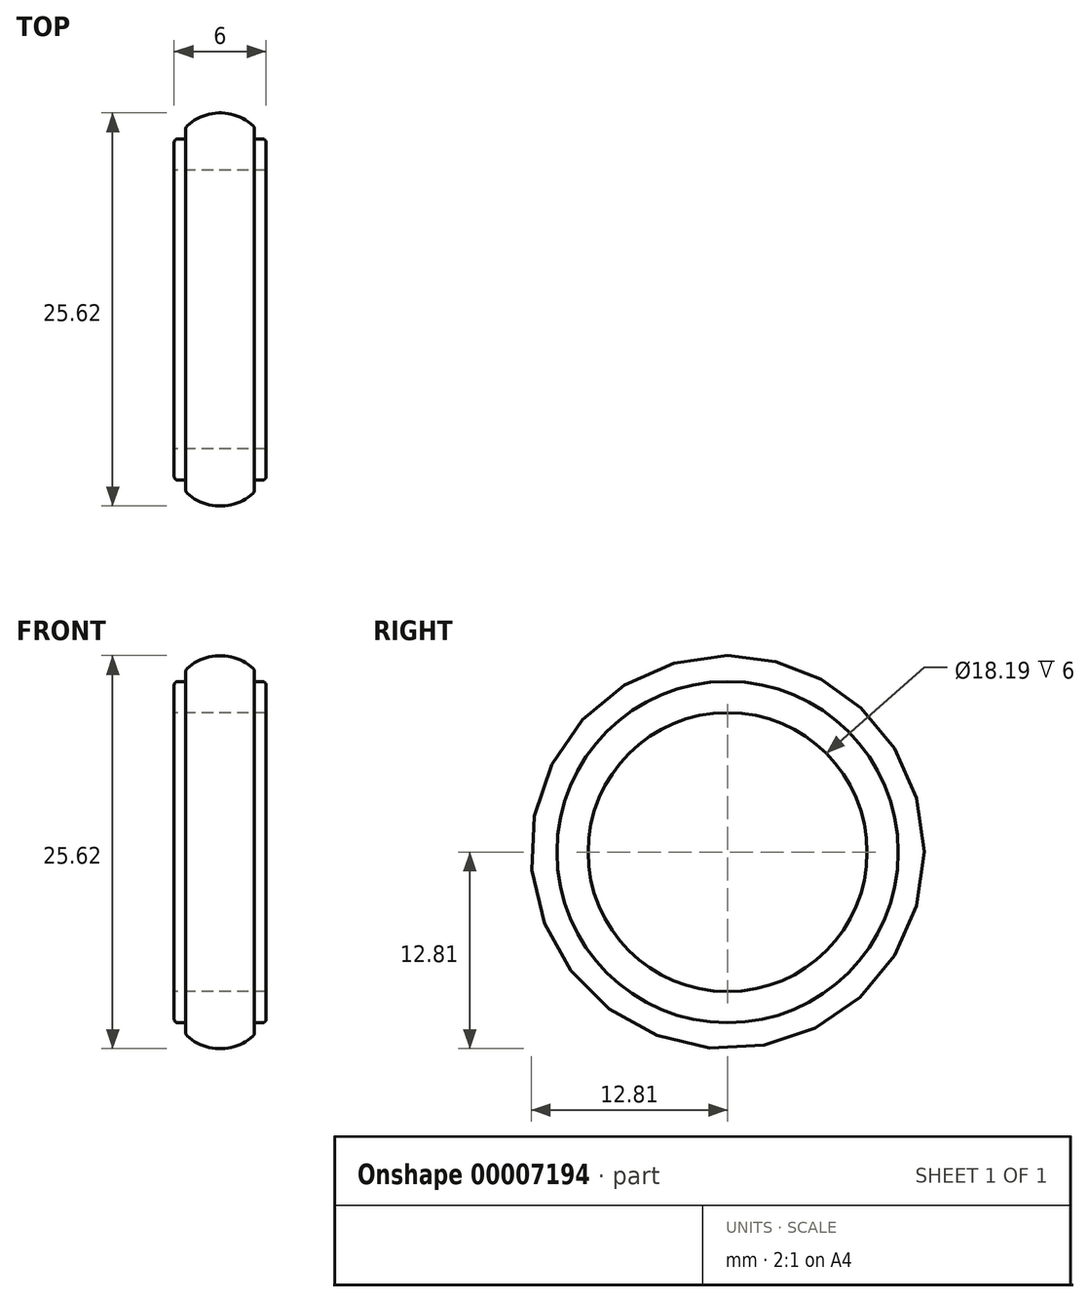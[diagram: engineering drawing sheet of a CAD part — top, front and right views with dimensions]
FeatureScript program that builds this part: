
annotation { "Feature Type Name" : "Feature", "Feature Type Description" : "" }
export const myFeature = defineFeature(function(context is Context, id is Id, definition is map)
    precondition{}
    {
        {
            var Q0;
            Q0=qCreatedBy(makeId("Front.planeOp"),FACE);
            var sketch = newSketch(context, id + "F0", { "sketchPlane" : qUnion([Q0])});
            skLineSegment(sketch, "E0", {"start": v(-3, 9.1) * mm, "end": v(3, 9.1) * mm});
            skLineSegment(sketch, "E1", {"start": v(-3, 9.1) * mm, "end": v(-3, 11.13) * mm});
            skLineSegment(sketch, "E2", {"start": v(3, 11.13) * mm, "end": v(3, 9.1) * mm});
            skLineSegment(sketch, "E3", {"start": v(-3, 11.13) * mm, "end": v(-2.24, 11.13) * mm});
            skLineSegment(sketch, "E4", {"start": v(-2.24, 11.13) * mm, "end": v(-2.24, 11.89) * mm});
            skLineSegment(sketch, "E5", {"start": v(2.24, 11.89) * mm, "end": v(2.24, 11.13) * mm});
            skLineSegment(sketch, "E6", {"start": v(2.24, 11.13) * mm, "end": v(3, 11.13) * mm});
            skArc(sketch, "E7", {"start": v(2.24, 11.89) * mm, "mid": v(0, 12.81) * mm, "end": v(-2.24, 11.89) * mm});
            skSolve(sketch);
        }
        {
            var Q0;
            Q0=qCreatedBy(makeId("Front.planeOp"),FACE);
            var sketch = newSketch(context, id + "F1", { "sketchPlane" : qUnion([Q0])});
            skLineSegment(sketch, "E8", {"start": v(-40.56, 0) * mm, "end": v(52.56, 0) * mm, "construction": true});
            skSolve(sketch);
        }
        {
            var Q0;
            Q0 = qSketchRegion(id + "F0", true);
            var Q1;
            Q1=sQuery(id+"F1.wireOp",EDGE,"E8");
            revolve(context, id + "F2", {"entities" : qUnion([Q0]), "axis" : qUnion([Q1]), "revolveType" : RevolveType.FULL});
        }
        {
            var Q0;
            Q0=makeQuery(id+"F2.opRevolve","SWEPT_EDGE",EDGE,{"disambiguationData":[OSD([sQuery(id+"F0.wireOp",EDGE,"E1"),sQuery(id+"F0.wireOp",EDGE,"E3")])]});
            var Q1;
            Q1=makeQuery(id+"F2.opRevolve","SWEPT_EDGE",EDGE,{"disambiguationData":[OSD([sQuery(id+"F0.wireOp",EDGE,"E4"),sQuery(id+"F0.wireOp",EDGE,"E7")])]});
            var Q2;
            Q2=makeQuery(id+"F2.opRevolve","SWEPT_EDGE",EDGE,{"disambiguationData":[OSD([sQuery(id+"F0.wireOp",EDGE,"E5"),sQuery(id+"F0.wireOp",EDGE,"E7")])]});
            var Q3;
            Q3=makeQuery(id+"F2.opRevolve","SWEPT_EDGE",EDGE,{"disambiguationData":[OSD([sQuery(id+"F0.wireOp",EDGE,"E2"),sQuery(id+"F0.wireOp",EDGE,"E6")])]});
            fillet(context, id + "F3", {"entities" : qUnion([Q0, Q1, Q2, Q3]), "radius" : 0.25 * mm, "allowEdgeOverflow" : false});
        }
    });
